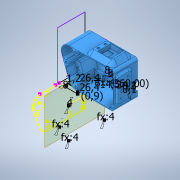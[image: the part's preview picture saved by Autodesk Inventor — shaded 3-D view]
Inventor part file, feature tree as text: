
AUTODESK INVENTOR PART (.ipt)
format: ipt  version: 2021.1 (Build 251245010, 245A)  size: 2,065,408 bytes
history: mixed  units: in
note: dims shown in document units (in); Inventor stores cm internally (conversion verified against a paired STEP export)
features: extrude x26, sketch x21, chamfer x9, move_body x9, direct_edit x7, projected_geometry x7, other x4, revolve x4, fillet x1, plane x1, imported_body x1
ambient origin geometry x8: Origin, YZ Plane, XZ Plane, XY Plane, X Axis, Y Axis, Z Axis, Center Point
bodies: Solid1 (imported_parasolid), Volumenkörper268 (imported_parasolid), Body1 (imported_parasolid)
feature tree (90):
  sketch  "Skizze1"  dims[d0=0.1575in d1=0.1575in]
  extrude  "Extrusion2"  Depth=0.1575in
  extrude  "Extrusion1"  Depth=0.1575in
  sketch  "Skizze3"  dims[d2=0.1575in d3=0.1575in]
  extrude  "Extrusion3"  Depth=0.252in TaperAngle=0.0deg
  extrude  "Extrusion4"  Depth=0.2756in TaperAngle=0.0deg
  extrude  "Extrusion5"  Depth=0.1575in
  extrude  "Extrusion6"  Depth=0.1575in
  direct_edit  "Direktbearbeitung2"
  extrude  "Extrusion8"  Depth=0.315in
  direct_edit  "Direktbearbeitung3"
  extrude  "Extrusion10"  Depth=0.1969in TaperAngle=0.0deg
  extrude  "Extrusion11"  TaperAngle=135.0deg  [1 undecoded]
  sketch  "Skizze16"  dims[d19=45.0deg d20=0.1969in d21=0.5906in d22=0.0in d23=0.0in]
  direct_edit  "Direktbearbeitung4"
  extrude  "Extrusion19"  TaperAngle=0.0deg  [1 undecoded]
  direct_edit  "Direktbearbeitung6"
  direct_edit  "Direktbearbeitung7"
  chamfer  "Fase2"  Distance=0.0157in
  extrude  "Extrusion26"  TaperAngle=135.0deg  [1 undecoded]
  chamfer  "Fase4"  Distance=0.3937in
  sketch  "Skizze29"  dims[d32=0.3937in d33=0.2362in d34=0.0in d35=0.0in d36=0.0in d37=0.0in d38=-0.0394in d39=0.0157in d40=0.0in]
  extrude  "Extrusion30"  TaperAngle=0.0deg  [1 undecoded]
  extrude  "Extrusion35"  Depth=1.0394in
  other  "Flächenverjüngung3"
  extrude  "Extrusion36"  Depth=0.0472in
  revolve  "Umdrehung1"
  sketch  "Skizze36"  dims[d45=0.3937in d46=0.0in d69=0.0in d70=0.0in d71=-0.2756in]
  fillet  "Rundung3"  Radius=0.315in
  extrude  "Extrusion37"  Depth=0.1181in TaperAngle=0.0deg
  chamfer  "Fase5"  [1 undecoded]
  plane  "Arbeitsebene2"
  extrude  "Extrusion38"  Depth=0.0197in
  extrude  "Extrusion39"  Depth=0.0197in
  extrude  "Extrusion40"  Depth=0.0197in TaperAngle=45.0deg
  chamfer  "Fase6"  Distance=0.0197in
  extrude  "Extrusion41"  Depth=0.1181in
  chamfer  "Fase7"  Distance=0.0197in
  extrude  "Extrusion42"  TaperAngle=90.0deg  [1 undecoded]
  extrude  "Extrusion9"  Depth=0.0787in
  direct_edit  "Direktbearbeitung8"
  sketch  "Skizze44"  dims[d122=0.0157in d123=0.0in d124=0.0197in d125=0.0787in d126=45.0deg d133=0.0197in d134=0.0in]
  sketch  "Skizze45"  dims[d144=0.3346in d145=0.0in d147=0.1181in]
  direct_edit  "Direktbearbeitung10"
  sketch  "Skizze47"  dims[d148=45.0deg d149=0.0197in d150=0.0in]
  extrude  "Extrusion43"  Depth=0.0787in TaperAngle=0.0deg
  extrude  "Extrusion44"  Depth=0.0787in TaperAngle=45.0deg
  chamfer  "Fase8"  Distance=0.3937in
  extrude  "Extrusion45"  Depth=0.0787in
  extrude  "Extrusion46"  Depth=1.9685in TaperAngle=0.0deg
  extrude  "Extrusion47"  Depth=0.1969in
  chamfer  "Fase9"  Distance=0.1969in
  chamfer  "Fase10"  Angle=135.0deg  [1 undecoded]
  chamfer  "Fase11"  Distance=0.0394in
  projected_geometry  "Projizierte Kontur2"
  sketch  "Skizze4"  dims[d4=0.1575in d5=0.252in d6=0.0in]
  sketch  "Skizze5"  dims[d7=0.2362in d8=0.0in d9=0.2756in d10=0.0in]
  sketch  "Skizze8"  dims[d11=0.1575in d12=0.0in d13=0.1575in]
  sketch  "Skizze9"  dims[d14=0.1575in d15=0.1575in]
  sketch  "Skizze10"  dims[d16=0.252in d17=0.0in d18=0.315in]
  sketch  "Skizze26"  dims[d30=0.315in d31=135.0deg]
  sketch  "Skizze35"  dims[d41=0.315in d42=135.0deg d43=0.3937in d44=0.0in]
  sketch  "Skizze37"  dims[d72=0.3937in d73=0.0in d74=1.0394in]
  projected_geometry  "Projizierte Kontur7"
  sketch  "Skizze38"  dims[d75=1.0394in d76=0.0472in d86=0.315in]
  sketch  "Skizze39"  dims[d87=0.2362in d88=0.0in d89=0.0in d90=0.1181in d104=0.0in d105=0.0in d106=-0.0787in]
  projected_geometry  "Projizierte Kontur8"
  sketch  "Skizze40"  dims[d109=0.0197in d113=0.0197in d114=0.0787in d115=45.0deg d119=0.0197in]
  projected_geometry  "Projizierte Kontur9"
  sketch  "Skizze41"  dims[d120=0.0197in d121=0.0197in]
  sketch  "Skizze48"  dims[d151=0.1969in d152=90.0deg d153=0.0787in d154=0.0787in d155=0.0in d156=0.0787in d157=0.0787in d158=45.0deg d159=0.3937in d160=0.0787in d161=1.9685in d162=0.0in d163=0.1969in d164=0.1969in d165=135.0deg d166=0.0394in d167=0.0in d168=0.1575in d172=0.1811in d173=0.252in d174=0.0in d175=0.0197in d176=0.0787in d177=45.0deg d178=0.1969in d179=0.1969in d180=0.0394in d181=0.0in d182=0.0197in d183=0.0787in d184=45.0deg d185=0.0157in d186=0.0in d187=-0.6184in d188=0.0in d189=2.8346in d190=0.0in d191=4.1339in d192=0.0in d193=0.0in d194=0.0in d195=0.0in d196=1.3346in d197=-1.0433in d198=0.0in d199=0.0in d201=180.0deg d202=3.9375in d203=0.1875in d204=0.375in d205=0.1575in d206=0.315in d207=0.3937in d208=0.0in d209=0.1969in d210=0.0354in d211=0.0in d212=0.0197in d213=0.0787in d214=45.0deg d215=0.2362in d216=0.0591in d217=0.0079in d218=0.0in d219=0.5709in d220=0.0354in d221=0.0039in d222=0.0039in d223=0.3937in d224=0.0in d225=0.0687in d226=0.0118in d227=0.0118in d228=1.5748in d230=360.0deg d232=0.3937in d233=0.0in d234=0.0118in d235=0.0787in d236=45.0deg d237=0.0039in d238=0.0787in d239=45.0deg d240=0.0118in d241=0.0787in d242=45.0deg]
  projected_geometry  "Projizierte Kontur11"
  projected_geometry  "Projizierte Kontur12"
  projected_geometry  "Projizierte Kontur13"
  other  "Löschen2"
  other  "Löschen3"
  move_body  "Verschieben1"
  other  "Löschen4"
  move_body  "Verschieben2"
  move_body  "Verschieben4"
  move_body  "Verschieben5"
  revolve  "Drehen1"  [1 undecoded]
  move_body  "Verschieben6"
  move_body  "Verschieben7"
  move_body  "Verschieben8"
  move_body  "Verschieben9"
  revolve  "Drehen3"  [1 undecoded]
  move_body  "Verschieben10"
  revolve  "Drehen4"  [1 undecoded]
  imported_body  NMx_Import_Brep_tag  [imported B-rep: ~9 faces, bbox_mm=[0.3, 9.566667, 0.3]]
note: 10 required parameter values undecoded (feature->parameter linkage not recoverable at this tier; creation-order binding heuristic only, values carry confidence <= 0.55)